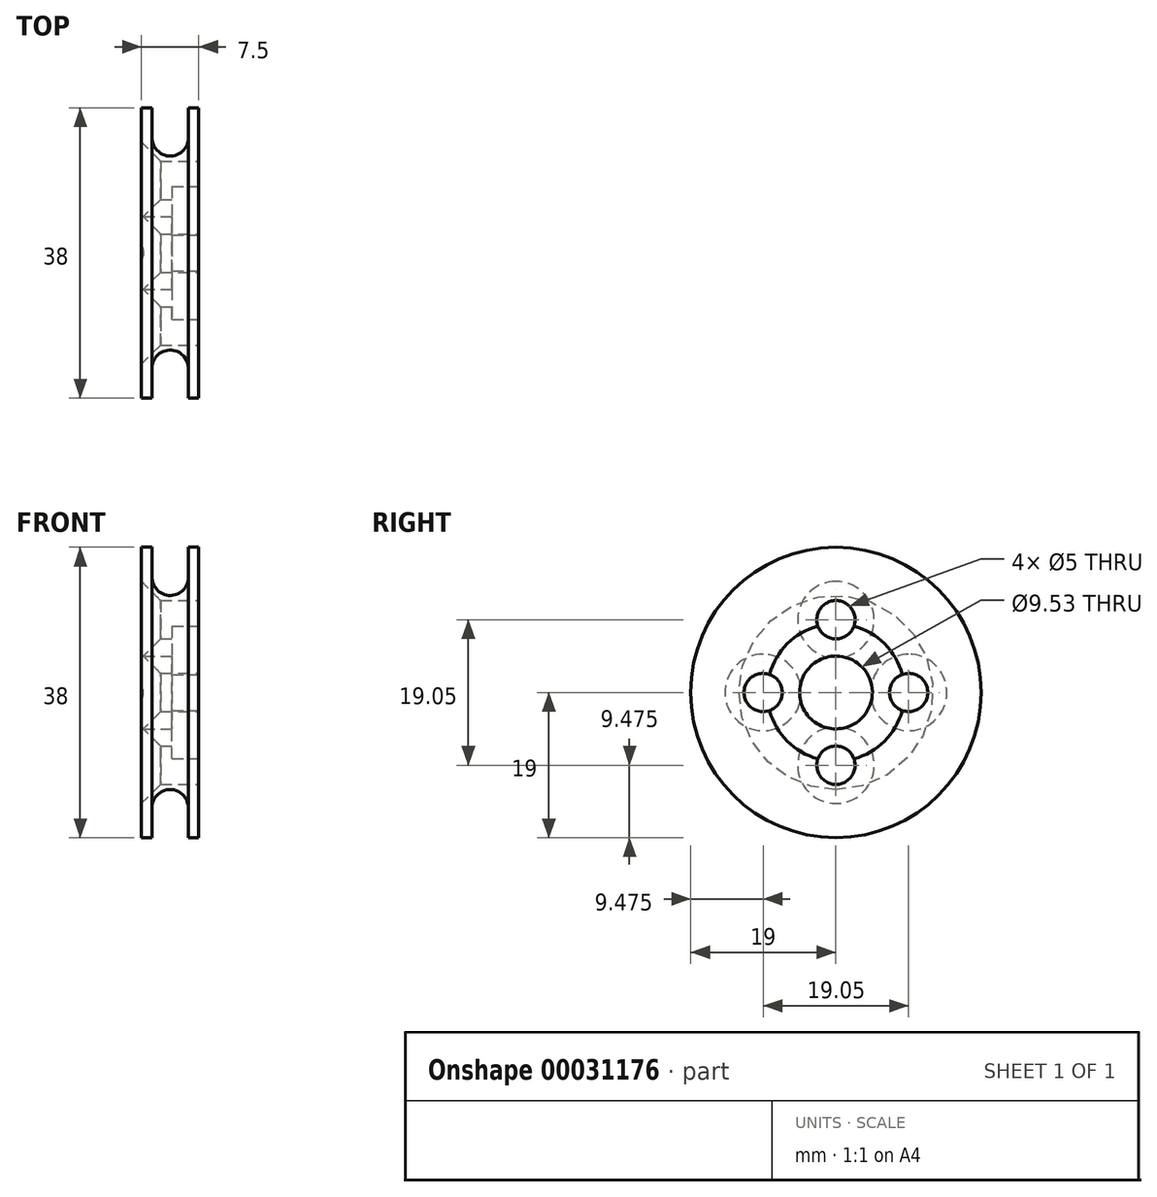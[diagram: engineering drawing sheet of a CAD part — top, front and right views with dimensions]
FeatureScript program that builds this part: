
annotation { "Feature Type Name" : "Feature", "Feature Type Description" : "" }
export const myFeature = defineFeature(function(context is Context, id is Id, definition is map)
    precondition{}
    {
        {
            var Q0;
            Q0=qCreatedBy(makeId("Front.planeOp"),FACE);
            var sketch = newSketch(context, id + "F0", { "sketchPlane" : qUnion([Q0])});
            skLineSegment(sketch, "E0", {"start": v(0, 0) * mm, "end": v(0, 19) * mm});
            skLineSegment(sketch, "E1", {"start": v(0, 19) * mm, "end": v(1.37, 19) * mm});
            skLineSegment(sketch, "E2", {"start": v(6.13, 19) * mm, "end": v(7.5, 19) * mm});
            skLineSegment(sketch, "E3", {"start": v(7.5, 19) * mm, "end": v(7.5, 9) * mm});
            skLineSegment(sketch, "E4", {"start": v(4, 0) * mm, "end": v(0, 0) * mm});
            skLineSegment(sketch, "E5", {"start": v(7.5, 9) * mm, "end": v(4, 9) * mm});
            skLineSegment(sketch, "E6", {"start": v(4, 9) * mm, "end": v(4, 0) * mm});
            skPoint(sketch, "E7.orphan", {"position": v(7.5, 0) * mm});
            skLineSegment(sketch, "E8", {"start": v(1.37, 19) * mm, "end": v(1.37, 15.08) * mm});
            skLineSegment(sketch, "E9", {"start": v(6.13, 19) * mm, "end": v(6.13, 15.08) * mm});
            skArc(sketch, "E10", {"start": v(1.37, 15.08) * mm, "mid": v(3.75, 12.7) * mm, "end": v(6.13, 15.08) * mm});
            skArc(sketch, "E11", {"start": v(6.13, 15.08) * mm, "mid": v(3.75, 17.46) * mm, "end": v(1.37, 15.08) * mm, "construction": true});
            skSolve(sketch);
        }
        {
            var Q0;
            Q0 = qSketchRegion(id + "F0", true);
            var Q1;
            Q1=sQuery(id+"F0.wireOp",EDGE,"E4");
            revolve(context, id + "F1", {"entities" : qUnion([Q0]), "axis" : qUnion([Q1]), "revolveType" : RevolveType.FULL});
        }
        {
            var Q0;
            Q0=makeQuery(id+"F1.opRevolve","SWEPT_FACE",FACE,{"disambiguationData":[OSD([sQuery(id+"F0.wireOp",EDGE,"E3")])]});
            var sketch = newSketch(context, id + "F2", { "sketchPlane" : qUnion([Q0])});
            skCircle(sketch, "E12", {"center": v(0, 0) * mm, "radius": 4.76 * mm});
            skCircle(sketch, "E13", {"center": v(0, 0) * mm, "radius": 9.53 * mm, "construction": true});
            skCircle(sketch, "E14", {"center": v(0, 9.53) * mm, "radius": 2.5 * mm});
            skCircle(sketch, "E15", {"center": v(9.53, 0) * mm, "radius": 2.5 * mm});
            skCircle(sketch, "E16", {"center": v(0, -9.53) * mm, "radius": 2.5 * mm});
            skCircle(sketch, "E17", {"center": v(-9.53, 0) * mm, "radius": 2.5 * mm});
            skSolve(sketch);
        }
        {
            var Q0;
            Q0 = qSketchRegion(id + "F2", true);
            extrude(context, id + "F3", {"entities" : qUnion([Q0]), "operationType" : NewBodyOperationType.REMOVE, "endBound" : BoundingType.THROUGH_ALL, "oppositeDirection" : true, "depth" : 25 * mm});
        }
        {
            var Q0;
            Q0=makeQuery(id+"F1.opRevolve","SWEPT_FACE",FACE,{"disambiguationData":[OSD([sQuery(id+"F0.wireOp",EDGE,"E0")])]});
            var sketch = newSketch(context, id + "F4", { "sketchPlane" : qUnion([Q0])});
            skPoint(sketch, "E18", {"position": v(0, 9.53) * mm});
            skPoint(sketch, "E19", {"position": v(9.53, 0) * mm});
            skPoint(sketch, "E20", {"position": v(0, -9.53) * mm});
            skPoint(sketch, "E21", {"position": v(-9.53, 0) * mm});
            skSolve(sketch);
        }
        {
            var Q0;
            Q0=sQuery(id+"F4.wireOp",VERTEX,"E18");
            var Q1;
            Q1=sQuery(id+"F4.wireOp",VERTEX,"E19");
            var Q2;
            Q2=sQuery(id+"F4.wireOp",VERTEX,"E20");
            var Q3;
            Q3=sQuery(id+"F4.wireOp",VERTEX,"E21");
            var Q4;
            Q4=makeQuery(id+"F1.opRevolve","SWEPT_BODY",BODY,{"disambiguationData":[OSD([sQuery(id+"F0.wireOp",EDGE,"E0"),sQuery(id+"F0.wireOp",EDGE,"E1"),sQuery(id+"F0.wireOp",EDGE,"E2"),sQuery(id+"F0.wireOp",EDGE,"E3"),sQuery(id+"F0.wireOp",EDGE,"E4"),sQuery(id+"F0.wireOp",EDGE,"E5"),sQuery(id+"F0.wireOp",EDGE,"E6"),sQuery(id+"F0.wireOp",EDGE,"E8"),sQuery(id+"F0.wireOp",EDGE,"E9"),sQuery(id+"F0.wireOp",EDGE,"E10")])]});
            hole(context, id + "F5", {"style" : HoleStyle.C_SINK, "holeDiameter" : 5 * mm, "cSinkDiameter" : 10 * mm, "endStyle" : HoleEndStyle.THROUGH, "locations" : qUnion([Q0, Q1, Q2, Q3]), "scope" : qUnion([Q4]), "cSinkAngle" : 90 * degree});
        }
    });
